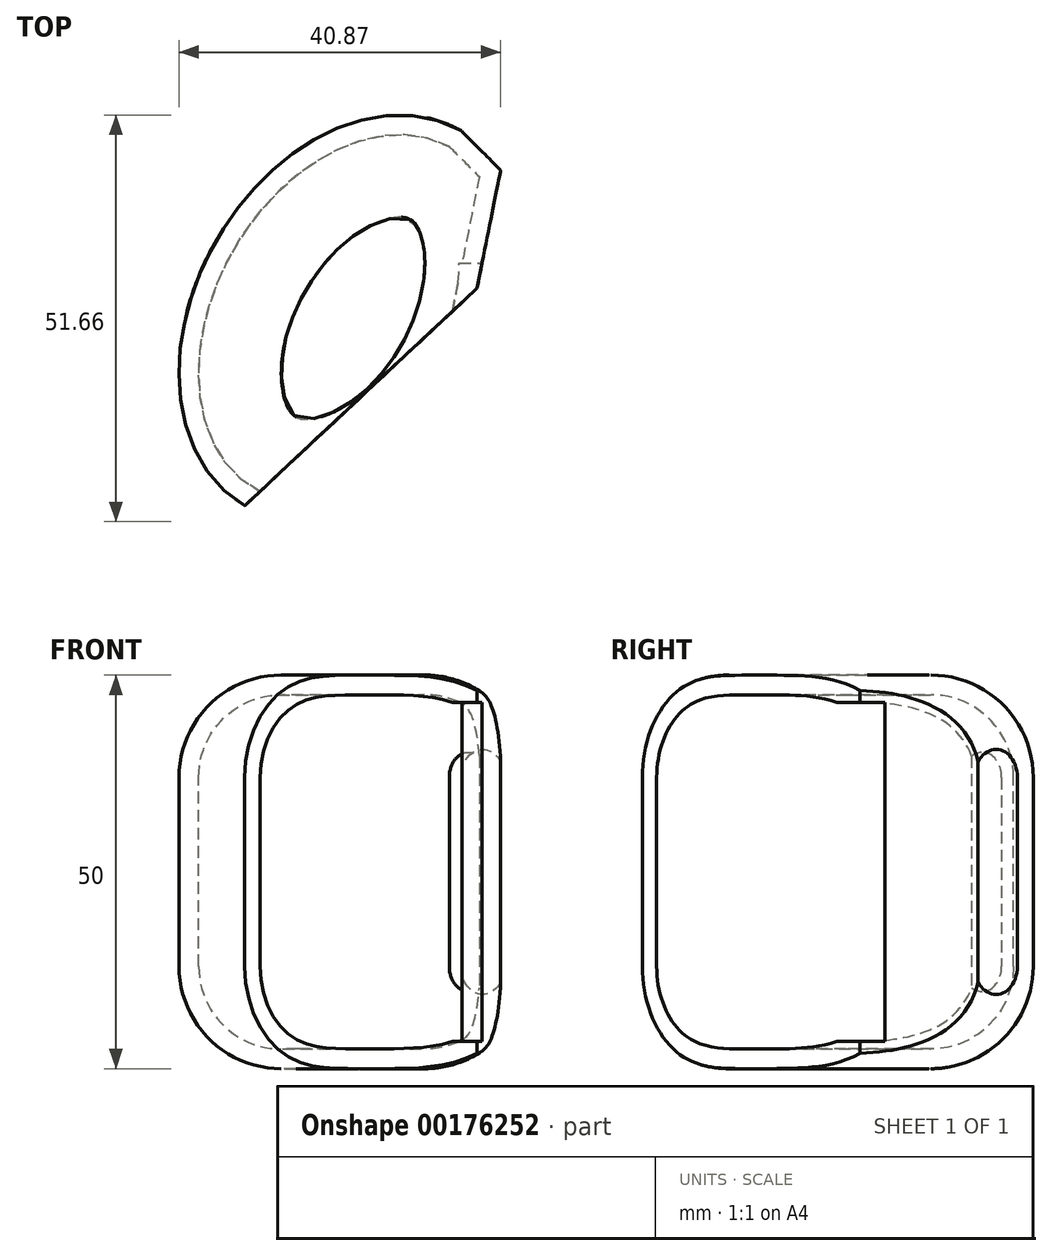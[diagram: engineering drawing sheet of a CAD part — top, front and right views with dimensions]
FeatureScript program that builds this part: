
annotation { "Feature Type Name" : "Feature", "Feature Type Description" : "" }
export const myFeature = defineFeature(function(context is Context, id is Id, definition is map)
    precondition{}
    {
        {
            var Q0;
            Q0=qCreatedBy(makeId("Top.planeOp"),FACE);
            var sketch = newSketch(context, id + "F0", { "sketchPlane" : qUnion([Q0])});
            skEllipticalArc(sketch, "E0", {});
            skPoint(sketch, "E1", {"position": v(13.75, 23.82) * mm});
            skPoint(sketch, "E2", {"position": v(-17.32, 10) * mm});
            skLineSegment(sketch, "E3", {"start": v(13.75, 23.82) * mm, "end": v(0, 0) * mm, "construction": true});
            skLineSegment(sketch, "E4", {"start": v(0, 0) * mm, "end": v(-13.75, -23.82) * mm, "construction": true});
            skLineSegment(sketch, "E5", {"start": v(13.75, 23.82) * mm, "end": v(18.75, 18.82) * mm});
            skLineSegment(sketch, "E6", {"start": v(18.75, 18.82) * mm, "end": v(15.75, 3.82) * mm});
            skLineSegment(sketch, "E7", {"start": v(15.75, 3.82) * mm, "end": v(-13.75, -23.82) * mm});
            const initialGuessF0  = {"E0": [0, 0, 0.5, 0.8660254037844386, 0.0275, 0.02, 0, 3.141592653589793]};
            skSetInitialGuess(sketch, initialGuessF0);
            skSolve(sketch);
        }
        {
            var Q0;
            Q0=qSketchRegion(id+"F0",true);
            extrude(context, id + "F1", {"entities" : qUnion([Q0]), "depth" : 25 * mm, "hasSecondDirection" : true, "secondDirectionOppositeDirection" : true, "secondDirectionDepth" : 25 * mm});
        }
        {
            var Q0;
            Q0=makeQuery(id+"F1.opExtrude","CAP_EDGE",EDGE,{"disambiguationData":[OSD([sQuery(id+"F0.wireOp",EDGE,"E0")])],"isStart":true});
            var Q1;
            Q1=makeQuery(id+"F1.opExtrude","CAP_EDGE",EDGE,{"disambiguationData":[OSD([sQuery(id+"F0.wireOp",EDGE,"E0")])],"isStart":false});
            fillet(context, id + "F2", {"entities" : qUnion([Q0, Q1]), "radius" : 13 * mm, "tangentPropagation" : true, "allowEdgeOverflow" : false});
        }
        {
            var Q0;
            Q0=makeQuery(id+"F1.opExtrude","SWEPT_FACE",FACE,{"disambiguationData":[OSD([sQuery(id+"F0.wireOp",EDGE,"E7")])]});
            shell(context, id + "F3", {"entities" : qUnion([Q0]), "thickness" : 2.5 * mm});
        }
        {
            var Q0;
            Q0=qCreatedBy(makeId("Front.planeOp"),FACE);
            var sketch = newSketch(context, id + "F4", { "sketchPlane" : qUnion([Q0])});
            skLineSegment(sketch, "E8.bottom", {"start": v(12.61, 21.55) * mm, "end": v(17.61, 21.55) * mm});
            skLineSegment(sketch, "E8.top", {"start": v(12.61, -21.55) * mm, "end": v(17.61, -21.55) * mm});
            skLineSegment(sketch, "E8.left", {"start": v(12.61, 21.55) * mm, "end": v(12.61, -21.55) * mm});
            skLineSegment(sketch, "E8.right", {"start": v(17.61, 21.55) * mm, "end": v(17.61, -21.55) * mm});
            skPoint(sketch, "E8.middle", {"position": v(15.11, 0) * mm});
            skSolve(sketch);
        }
        {
            var Q0;
            Q0=qSketchRegion(id+"F4",true);
            extrude(context, id + "F5", {"entities" : qUnion([Q0]), "operationType" : NewBodyOperationType.REMOVE, "oppositeDirection" : true, "depth" : 7 * mm, "hasSecondDirection" : true, "secondDirectionOppositeDirection" : false, "secondDirectionDepth" : 5 * mm});
        }
    });
